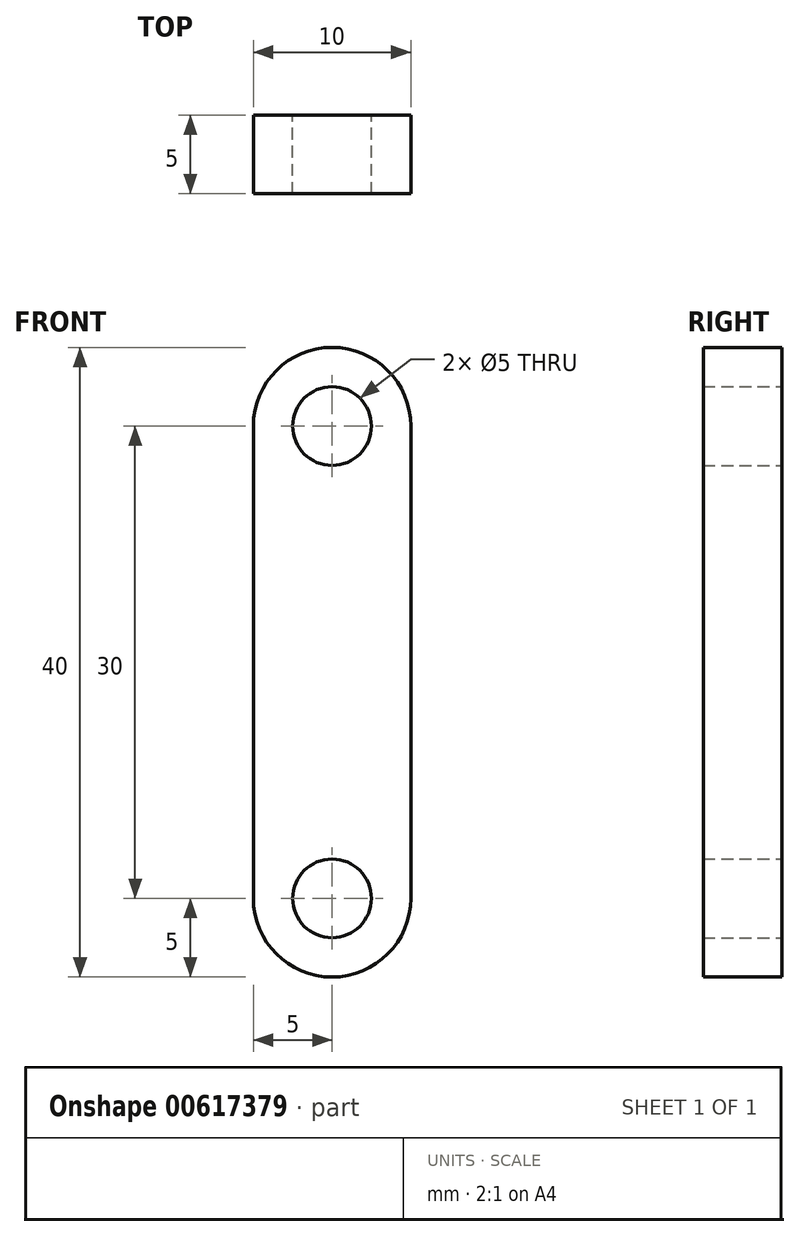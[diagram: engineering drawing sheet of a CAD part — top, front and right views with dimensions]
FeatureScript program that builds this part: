
annotation { "Feature Type Name" : "Feature", "Feature Type Description" : "" }
export const myFeature = defineFeature(function(context is Context, id is Id, definition is map)
    precondition{}
    {
        {
            var Q0;
            Q0=qCreatedBy(makeId("Front.planeOp"),FACE);
            var sketch = newSketch(context, id + "F0", { "sketchPlane" : qUnion([Q0])});
            skArc(sketch, "E0", {"start": v(-5, 0) * mm, "mid": v(0, -5) * mm, "end": v(5, 0) * mm});
            skArc(sketch, "E1", {"start": v(5, 30) * mm, "mid": v(0, 35) * mm, "end": v(-5, 30) * mm});
            skLineSegment(sketch, "E2", {"start": v(-5, 30) * mm, "end": v(-5, 0) * mm});
            skLineSegment(sketch, "E3", {"start": v(5, 30) * mm, "end": v(5, 0) * mm});
            skCircle(sketch, "E4", {"center": v(0, 0) * mm, "radius": 2.5 * mm});
            skCircle(sketch, "E5", {"center": v(0, 30) * mm, "radius": 2.5 * mm});
            skSolve(sketch);
        }
        {
            var Q0;
            Q0=makeQuery(id+"F0.imprint","IMPRINT",FACE,{"disambiguationData":[TD([[makeQuery(id+"F0.imprint","IMPRINT",EDGE,{"derivedFrom":sQuery(id+"F0.wireOp",EDGE,"E0")}),1.0]])]});
            extrude(context, id + "F1", {"entities" : qUnion([Q0]), "depth" : 5 * mm, "offsetDistance" : 25 * mm});
        }
    });
